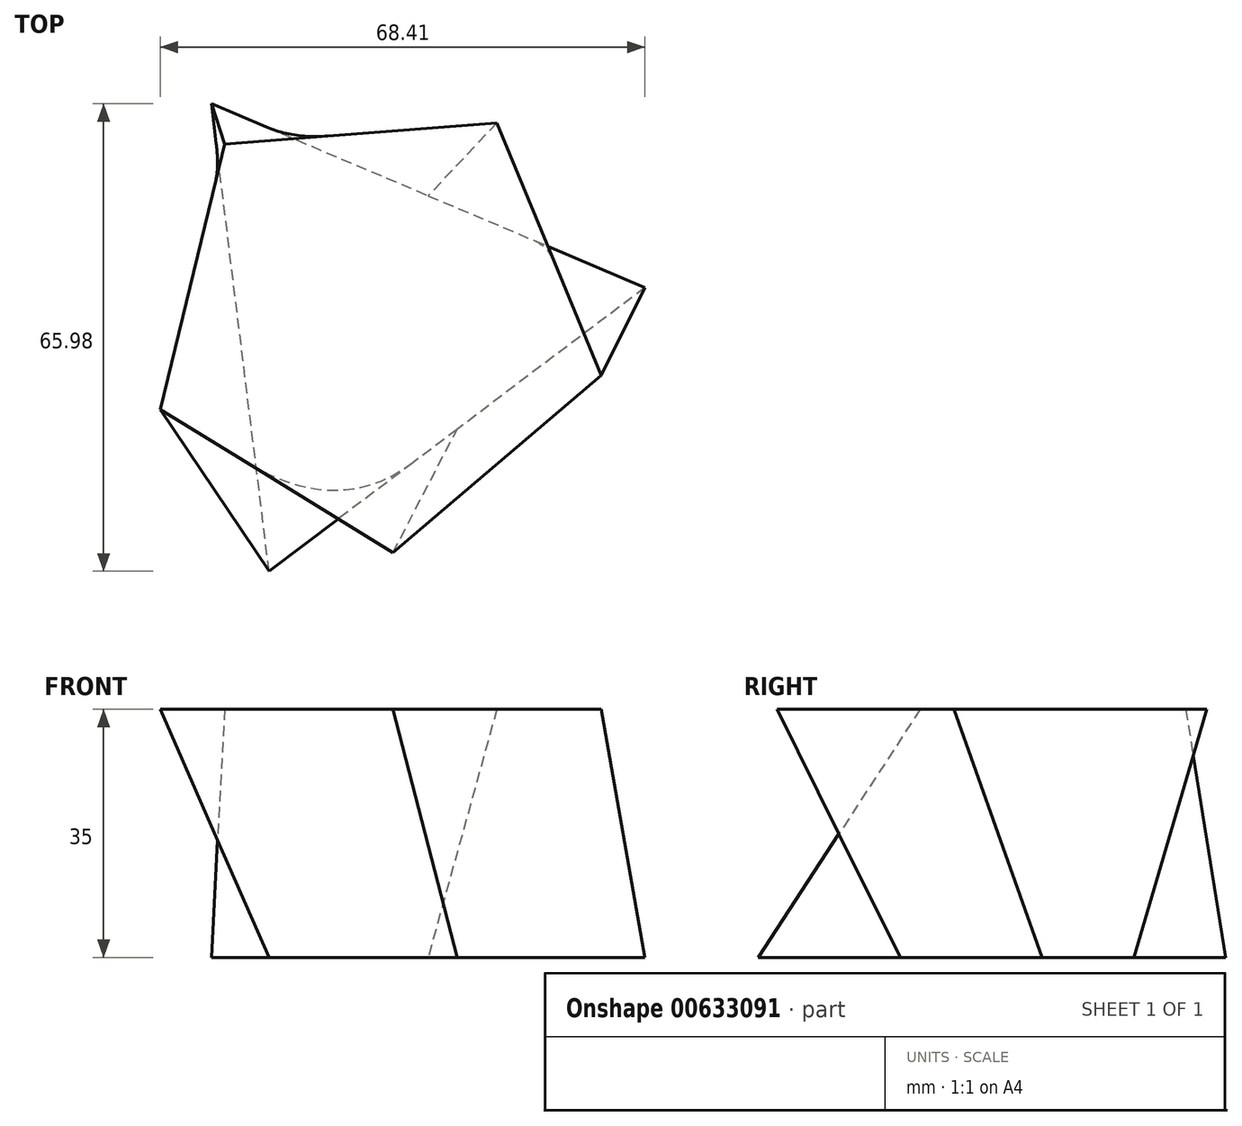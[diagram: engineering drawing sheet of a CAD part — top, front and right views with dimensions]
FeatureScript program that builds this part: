
annotation { "Feature Type Name" : "Feature", "Feature Type Description" : "" }
export const myFeature = defineFeature(function(context is Context, id is Id, definition is map)
    precondition{}
    {
        {
            var Q0;
            Q0=qCreatedBy(makeId("Top.planeOp"),FACE);
            cPlane(context, id + "F0", {"entities" : qUnion([Q0]), "cplaneType" : CPlaneType.OFFSET, "offset" : 35 * mm, "width" : 150 * mm, "height" : 150 * mm});
        }
        {
            var Q0;
            Q0=qCreatedBy(makeId("Top.planeOp"),FACE);
            var sketch = newSketch(context, id + "F1", { "sketchPlane" : qUnion([Q0])});
            skCircle(sketch, "E0.cCircle", {"center": v(0, 0) * mm, "radius": 19.19 * mm, "construction": true});
            skLineSegment(sketch, "E0.0", {"start": v(38.09, 4.7) * mm, "end": v(-14.97, -35.34) * mm});
            skLineSegment(sketch, "E0.1", {"start": v(-14.97, -35.34) * mm, "end": v(-23.12, 30.64) * mm});
            skLineSegment(sketch, "E0.2", {"start": v(-23.12, 30.64) * mm, "end": v(38.09, 4.7) * mm});
            skPoint(sketch, "E0.0.midPoint", {"position": v(11.56, -15.32) * mm});
            skSolve(sketch);
        }
        {
            var Q0;
            Q0=qCreatedBy(id+"F0.planeOp",FACE);
            var sketch = newSketch(context, id + "F2", { "sketchPlane" : qUnion([Q0])});
            skCircle(sketch, "E1.cCircle", {"center": v(0, 0) * mm, "radius": 26.53 * mm, "construction": true});
            skLineSegment(sketch, "E1.0", {"start": v(31.88, -7.7) * mm, "end": v(2.52, -32.7) * mm});
            skLineSegment(sketch, "E1.1", {"start": v(2.52, -32.7) * mm, "end": v(-30.32, -12.5) * mm});
            skLineSegment(sketch, "E1.2", {"start": v(-30.32, -12.5) * mm, "end": v(-21.26, 24.97) * mm});
            skLineSegment(sketch, "E1.3", {"start": v(-21.26, 24.97) * mm, "end": v(17.18, 27.93) * mm});
            skLineSegment(sketch, "E1.4", {"start": v(17.18, 27.93) * mm, "end": v(31.88, -7.7) * mm});
            skPoint(sketch, "E1.0.midPoint", {"position": v(17.2, -20.2) * mm});
            skSolve(sketch);
        }
        {
            var Q0;
            Q0=makeQuery(id+"F2.imprint","IMPRINT",FACE,{"disambiguationData":[TD([[makeQuery(id+"F2.imprint","IMPRINT",EDGE,{"derivedFrom":sQuery(id+"F2.wireOp",EDGE,"E1.0")}),-1.0]])]});
            var Q1;
            Q1=makeQuery(id+"F1.imprint","IMPRINT",FACE,{"disambiguationData":[TD([[makeQuery(id+"F1.imprint","IMPRINT",EDGE,{"derivedFrom":sQuery(id+"F1.wireOp",EDGE,"E0.0")}),-1.0]])]});
            loft(context, id + "F3", {"sheetProfilesArray" : [{ "sheetProfileEntities" : qUnion([Q0]) }, { "sheetProfileEntities" : qUnion([Q1]) }]});
        }
    });
